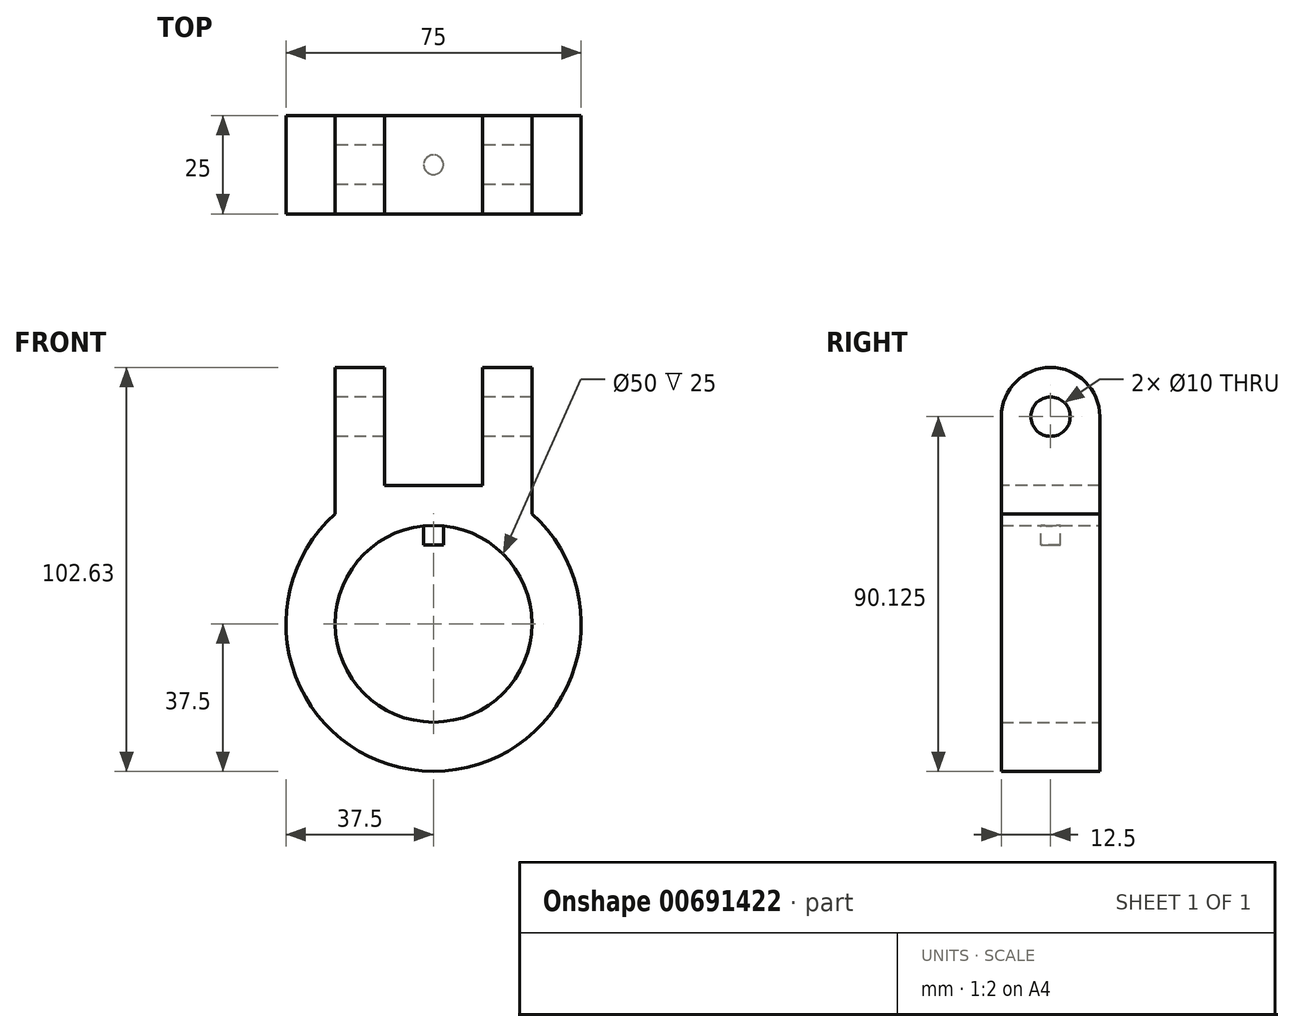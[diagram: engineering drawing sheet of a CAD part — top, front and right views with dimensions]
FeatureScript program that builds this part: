
annotation { "Feature Type Name" : "Feature", "Feature Type Description" : "" }
export const myFeature = defineFeature(function(context is Context, id is Id, definition is map)
    precondition{}
    {
        {
            var Q0;
            Q0=qCreatedBy(makeId("Front.planeOp"),FACE);
            var sketch = newSketch(context, id + "F0", { "sketchPlane" : qUnion([Q0])});
            skCircle(sketch, "E0", {"center": v(0, 0) * mm, "radius": 25 * mm});
            skCircle(sketch, "E1", {"center": v(0, 0) * mm, "radius": 37.5 * mm});
            skSolve(sketch);
        }
        {
            var Q0;
            Q0 = qSketchRegion(id + "F0", true);
            extrude(context, id + "F1", {"entities" : qUnion([Q0]), "depth" : 5 * mm, "offsetDistance" : 25 * mm});
        }
        {
            var Q0;
            Q0=qCreatedBy(makeId("Front.planeOp"),FACE);
            var sketch = newSketch(context, id + "F2", { "sketchPlane" : qUnion([Q0])});
            skLineSegment(sketch, "E2.bottom", {"start": v(2.5, 30) * mm, "end": v(-2.5, 30) * mm});
            skLineSegment(sketch, "E2.top", {"start": v(2.5, 20) * mm, "end": v(-2.5, 20) * mm});
            skLineSegment(sketch, "E2.left", {"start": v(2.5, 30) * mm, "end": v(2.5, 20) * mm});
            skLineSegment(sketch, "E2.right", {"start": v(-2.5, 30) * mm, "end": v(-2.5, 20) * mm});
            skPoint(sketch, "E2.middle", {"position": v(0, 25) * mm});
            skSolve(sketch);
        }
        {
            var Q0;
            Q0 = qSketchRegion(id + "F2", true);
            extrude(context, id + "F3", {"entities" : qUnion([Q0]), "operationType" : NewBodyOperationType.ADD, "depth" : 5 * mm, "offsetDistance" : 25 * mm});
        }
        {
            var Q0;
            Q0=makeQuery(id+"F3.opExtrude","CAP_EDGE",EDGE,{"disambiguationData":[OSD([sQuery(id+"F2.wireOp",EDGE,"E2.right")])],"isStart":false});
            var Q1;
            Q1=makeQuery(id+"F3.opExtrude","CAP_EDGE",EDGE,{"disambiguationData":[OSD([sQuery(id+"F2.wireOp",EDGE,"E2.left")])],"isStart":false});
            var Q2;
            Q2=makeQuery(id+"F3.opExtrude","CAP_EDGE",EDGE,{"disambiguationData":[OSD([sQuery(id+"F2.wireOp",EDGE,"E2.right")])],"isStart":true});
            var Q3;
            Q3=makeQuery(id+"F3.opExtrude","CAP_EDGE",EDGE,{"disambiguationData":[OSD([sQuery(id+"F2.wireOp",EDGE,"E2.left")])],"isStart":true});
            fillet(context, id + "F4", {"entities" : qUnion([Q0, Q1, Q2, Q3]), "radius" : 2.5 * mm, "tangentPropagation" : true, "allowEdgeOverflow" : false});
        }
        {
            var Q0;
            Q0=makeQuery(id+"F3.boolean.opBoolean","MERGE",FACE,{"derivedFrom":[makeQuery(id+"F1.opExtrude","CAP_FACE",FACE,{"disambiguationData":[OSD([sQuery(id+"F0.wireOp",EDGE,"E0"),sQuery(id+"F0.wireOp",EDGE,"E1")])],"isStart":false}),makeQuery(id+"F3.opExtrude","CAP_FACE",FACE,{"disambiguationData":[OSD([sQuery(id+"F2.wireOp",EDGE,"E2.bottom"),sQuery(id+"F2.wireOp",EDGE,"E2.top"),sQuery(id+"F2.wireOp",EDGE,"E2.left"),sQuery(id+"F2.wireOp",EDGE,"E2.right")])],"isStart":false})]});
            var sketch = newSketch(context, id + "F5", { "sketchPlane" : qUnion([Q0])});
            skCircle(sketch, "E3", {"center": v(0, 0) * mm, "radius": 37.5 * mm});
            skCircle(sketch, "E4", {"center": v(0, 0) * mm, "radius": 25 * mm});
            skSolve(sketch);
        }
        {
            var Q0;
            Q0 = qSketchRegion(id + "F5", true);
            extrude(context, id + "F6", {"entities" : qUnion([Q0]), "operationType" : NewBodyOperationType.ADD, "depth" : 10 * mm, "offsetDistance" : 25 * mm, "hasSecondDirection" : true, "secondDirectionOppositeDirection" : true, "secondDirectionDepth" : 15 * mm});
        }
        {
            var Q0;
            Q0=qCreatedBy(makeId("Front.planeOp"),FACE);
            var sketch = newSketch(context, id + "F7", { "sketchPlane" : qUnion([Q0])});
            skLineSegment(sketch, "E5.bottom", {"start": v(25, 65.13) * mm, "end": v(-25, 65.13) * mm});
            skLineSegment(sketch, "E5.top", {"start": v(25, 25.13) * mm, "end": v(-25, 25.13) * mm});
            skLineSegment(sketch, "E5.left", {"start": v(25, 65.13) * mm, "end": v(25, 25.13) * mm});
            skLineSegment(sketch, "E5.right", {"start": v(-25, 65.13) * mm, "end": v(-25, 25.13) * mm});
            skPoint(sketch, "E5.middle", {"position": v(0, 45.13) * mm});
            skSolve(sketch);
        }
        {
            var Q0;
            Q0 = qSketchRegion(id + "F7", true);
            extrude(context, id + "F8", {"entities" : qUnion([Q0]), "operationType" : NewBodyOperationType.ADD, "depth" : 15 * mm, "offsetDistance" : 25 * mm, "hasSecondDirection" : true, "secondDirectionOppositeDirection" : true, "secondDirectionDepth" : 10 * mm});
        }
        {
            var Q0;
            Q0=makeQuery(id+"F8.boolean.opBoolean","MERGE",FACE,{"derivedFrom":[makeQuery(id+"F6.opExtrude","CAP_FACE",FACE,{"disambiguationData":[OSD([sQuery(id+"F5.wireOp",EDGE,"E3"),sQuery(id+"F5.wireOp",EDGE,"E4")])],"isStart":false}),makeQuery(id+"F8.opExtrude","CAP_FACE",FACE,{"disambiguationData":[OSD([sQuery(id+"F7.wireOp",EDGE,"E5.bottom"),sQuery(id+"F7.wireOp",EDGE,"E5.top"),sQuery(id+"F7.wireOp",EDGE,"E5.left"),sQuery(id+"F7.wireOp",EDGE,"E5.right")])],"isStart":false})]});
            var sketch = newSketch(context, id + "F9", { "sketchPlane" : qUnion([Q0])});
            skLineSegment(sketch, "E6.bottom", {"start": v(-12.5, 65.13) * mm, "end": v(12.5, 65.13) * mm});
            skLineSegment(sketch, "E6.top", {"start": v(-12.5, 35.13) * mm, "end": v(12.5, 35.13) * mm});
            skLineSegment(sketch, "E6.left", {"start": v(-12.5, 65.13) * mm, "end": v(-12.5, 35.13) * mm});
            skLineSegment(sketch, "E6.right", {"start": v(12.5, 65.13) * mm, "end": v(12.5, 35.13) * mm});
            skSolve(sketch);
        }
        {
            var Q0;
            Q0=makeQuery(id+"F9.imprint","IMPRINT",FACE,{"disambiguationData":[TD([[makeQuery(id+"F9.imprint","IMPRINT",EDGE,{"derivedFrom":sQuery(id+"F9.wireOp",EDGE,"E6.bottom")}),1.0]])]});
            extrude(context, id + "F10", {"entities" : qUnion([Q0]), "operationType" : NewBodyOperationType.REMOVE, "oppositeDirection" : true, "depth" : 25 * mm, "offsetDistance" : 25 * mm});
        }
        {
            var Q0;
            {var subQ0=sQuery(id+"F7.wireOp",EDGE,"E5.right");var subQ1=sQuery(id+"F7.wireOp",EDGE,"E5.bottom");Q0=makeQuery(id+"F10.boolean.opBoolean","SPLIT",EDGE,{"disambiguationData":[TD([makeQuery(id+"F8.opExtrude","SWEPT_FACE",FACE,{"disambiguationData":[OSD([subQ0])]})])],"derivedFrom":makeQuery(id+"F8.opExtrude","CAP_EDGE",EDGE,{"disambiguationData":[OSD([subQ1])],"isStart":true})});}
            var Q1;
            {var subQ0=sQuery(id+"F7.wireOp",EDGE,"E5.right");var subQ1=sQuery(id+"F7.wireOp",EDGE,"E5.bottom");Q1=makeQuery(id+"F10.boolean.opBoolean","SPLIT",EDGE,{"disambiguationData":[TD([makeQuery(id+"F8.opExtrude","SWEPT_FACE",FACE,{"disambiguationData":[OSD([subQ0])]})])],"derivedFrom":makeQuery(id+"F8.opExtrude","CAP_EDGE",EDGE,{"disambiguationData":[OSD([subQ1])],"isStart":false})});}
            var Q2;
            {var subQ0=sQuery(id+"F7.wireOp",EDGE,"E5.left");var subQ1=sQuery(id+"F7.wireOp",EDGE,"E5.bottom");Q2=makeQuery(id+"F10.boolean.opBoolean","SPLIT",EDGE,{"disambiguationData":[TD([makeQuery(id+"F8.opExtrude","SWEPT_FACE",FACE,{"disambiguationData":[OSD([subQ0])]})])],"derivedFrom":makeQuery(id+"F8.opExtrude","CAP_EDGE",EDGE,{"disambiguationData":[OSD([subQ1])],"isStart":false})});}
            var Q3;
            {var subQ0=sQuery(id+"F7.wireOp",EDGE,"E5.left");var subQ1=sQuery(id+"F7.wireOp",EDGE,"E5.bottom");Q3=makeQuery(id+"F10.boolean.opBoolean","SPLIT",EDGE,{"disambiguationData":[TD([makeQuery(id+"F8.opExtrude","SWEPT_FACE",FACE,{"disambiguationData":[OSD([subQ0])]})])],"derivedFrom":makeQuery(id+"F8.opExtrude","CAP_EDGE",EDGE,{"disambiguationData":[OSD([subQ1])],"isStart":true})});}
            fillet(context, id + "F11", {"entities" : qUnion([Q0, Q1, Q2, Q3]), "radius" : 12.5 * mm, "tangentPropagation" : true, "allowEdgeOverflow" : false});
        }
        {
            var Q0;
            Q0=makeQuery(id+"F8.opExtrude","SWEPT_FACE",FACE,{"disambiguationData":[OSD([sQuery(id+"F7.wireOp",EDGE,"E5.right")])]});
            var sketch = newSketch(context, id + "F12", { "sketchPlane" : qUnion([Q0])});
            skCircle(sketch, "E7", {"center": v(2.5, 52.63) * mm, "radius": 5 * mm});
            skSolve(sketch);
        }
        {
            var Q0;
            Q0 = qSketchRegion(id + "F12", true);
            extrude(context, id + "F13", {"entities" : qUnion([Q0]), "operationType" : NewBodyOperationType.REMOVE, "endBound" : BoundingType.THROUGH_ALL, "oppositeDirection" : true, "depth" : 25 * mm, "offsetDistance" : 25 * mm});
        }
    });
